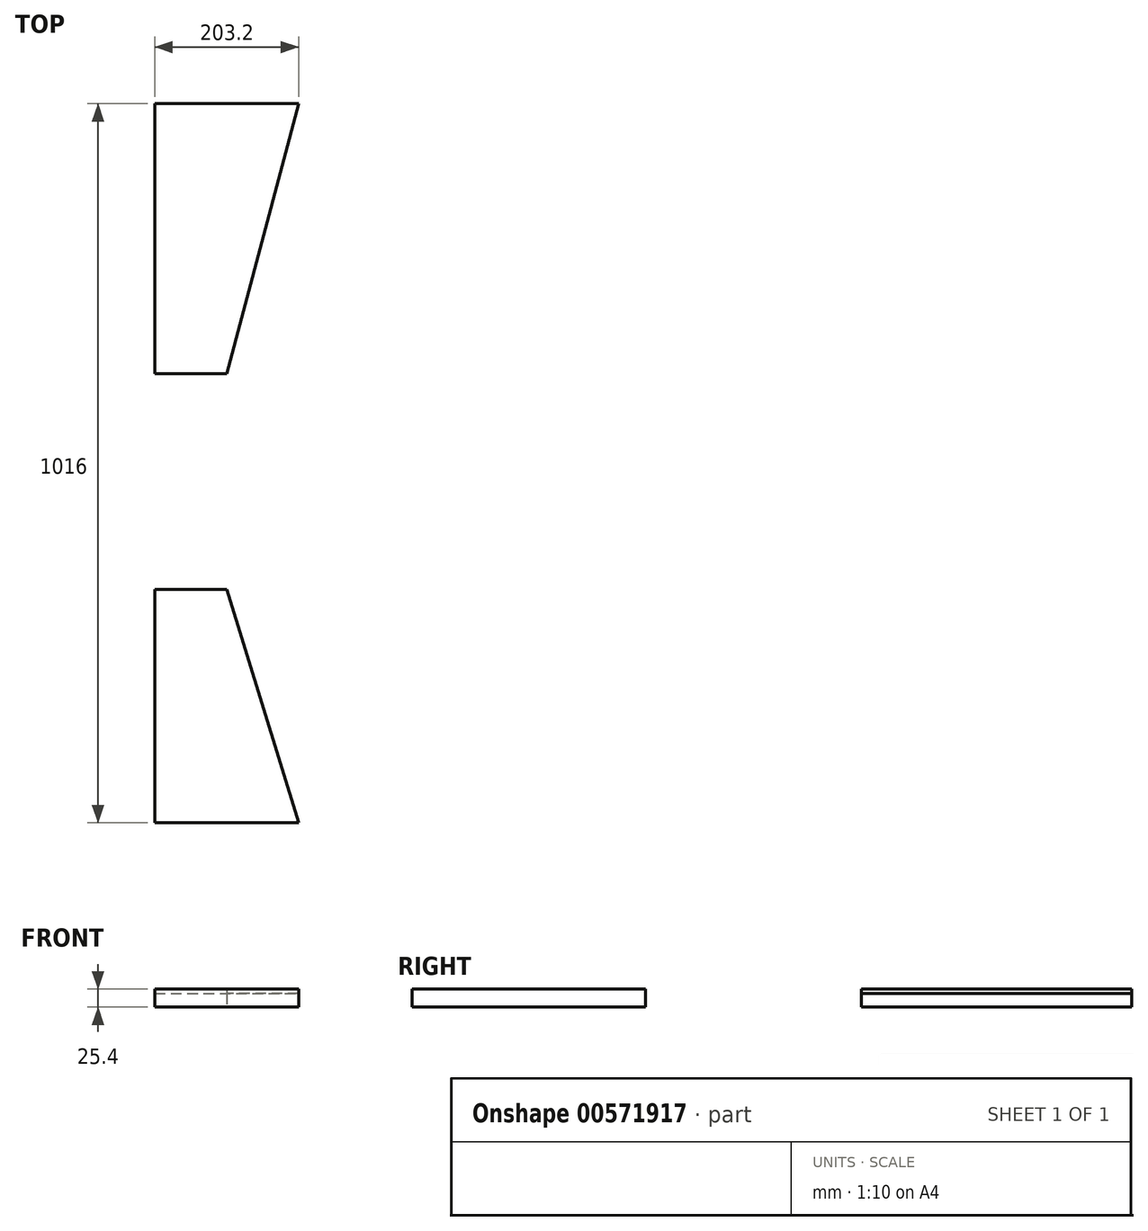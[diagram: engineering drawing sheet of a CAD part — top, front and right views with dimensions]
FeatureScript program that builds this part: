
annotation { "Feature Type Name" : "Feature", "Feature Type Description" : "" }
export const myFeature = defineFeature(function(context is Context, id is Id, definition is map)
    precondition{}
    {
        {
            var Q0;
            Q0=qCreatedBy(makeId("Top.planeOp"),FACE);
            var sketch = newSketch(context, id + "F0", { "sketchPlane" : qUnion([Q0])});
            skLineSegment(sketch, "E0.bottom", {"start": v(52.75, 0) * mm, "end": v(255.95, 0) * mm});
            skLineSegment(sketch, "E0.top", {"start": v(52.75, -1016) * mm, "end": v(255.95, -1016) * mm});
            skLineSegment(sketch, "E0.left", {"start": v(52.75, 0) * mm, "end": v(52.75, -1016) * mm});
            skLineSegment(sketch, "E0.right", {"start": v(255.95, 0) * mm, "end": v(255.95, -1016) * mm});
            skCircle(sketch, "E1", {"center": v(154.22, -482.6) * mm, "radius": 9.52 * mm});
            skCircle(sketch, "E2", {"center": v(154.22, -584.2) * mm, "radius": 9.53 * mm});
            skLineSegment(sketch, "E3.bottom", {"start": v(255.95, -1016) * mm, "end": v(154.22, -1016) * mm});
            skLineSegment(sketch, "E3.left", {"start": v(255.95, -1016) * mm, "end": v(255.95, -686.23) * mm});
            skLineSegment(sketch, "E4.bottom", {"start": v(255.95, 0) * mm, "end": v(154.22, 0) * mm});
            skLineSegment(sketch, "E4.left", {"start": v(255.95, 0) * mm, "end": v(255.95, -381.43) * mm});
            skLineSegment(sketch, "E5.top", {"start": v(52.75, -381.43) * mm, "end": v(255.95, -381.43) * mm});
            skLineSegment(sketch, "E5.left", {"start": v(52.75, 0) * mm, "end": v(52.75, -381.43) * mm});
            skLineSegment(sketch, "E6.bottom", {"start": v(255.95, -686.23) * mm, "end": v(52.75, -686.23) * mm});
            skLineSegment(sketch, "E6.top", {"start": v(255.95, -1016) * mm, "end": v(52.75, -1016) * mm});
            skLineSegment(sketch, "E6.left", {"start": v(255.95, -686.23) * mm, "end": v(255.95, -1016) * mm});
            skLineSegment(sketch, "E6.right", {"start": v(52.75, -686.23) * mm, "end": v(52.75, -1016) * mm});
            skLineSegment(sketch, "E7", {"start": v(255.95, 0) * mm, "end": v(154.35, -381.43) * mm});
            skLineSegment(sketch, "E8", {"start": v(255.95, -1016) * mm, "end": v(154.35, -686.23) * mm});
            skSolve(sketch);
        }
        {
            var Q0;
            Q0=makeQuery(id+"F0.imprint","IMPRINT",FACE,{"disambiguationData":[TD([[makeQuery(id+"F0.imprint","IMPRINT",EDGE,{"derivedFrom":sQuery(id+"F0.wireOp",EDGE,"E0.bottom")}),-1.0]])]});
            extrude(context, id + "F1", {"entities" : qUnion([Q0]), "depth" : 19.05 * mm, "offsetDistance" : 25.4 * mm});
        }
        {
            var Q0;
            {var subQ0=sQuery(id+"F0.wireOp",EDGE,"E5.left");Q0=makeQuery(id+"F0.imprint","IMPRINT",FACE,{"disambiguationData":[TD([[makeQuery(id+"F0.imprint","IMPRINT",EDGE,{"derivedFrom":subQ0}),1.0]])]});}
            var Q1;
            {var subQ0=sQuery(id+"F0.wireOp",EDGE,"E6.right");Q1=makeQuery(id+"F0.imprint","IMPRINT",FACE,{"disambiguationData":[TD([[makeQuery(id+"F0.imprint","IMPRINT",EDGE,{"derivedFrom":subQ0}),1.0]])]});}
            var Q2;
            {var subQ1=sQuery(id+"F0.wireOp",EDGE,"E0.left");Q2=makeQuery(id+"F0.imprint","IMPRINT",FACE,{"disambiguationData":[TD([[makeQuery(id+"F0.imprint","IMPRINT",EDGE,{"derivedFrom":subQ1}),1.0]])]});}
            extrude(context, id + "F2", {"entities" : qUnion([Q0, Q1, Q2]), "depth" : 25.4 * mm, "offsetDistance" : 25.4 * mm});
        }
    });
